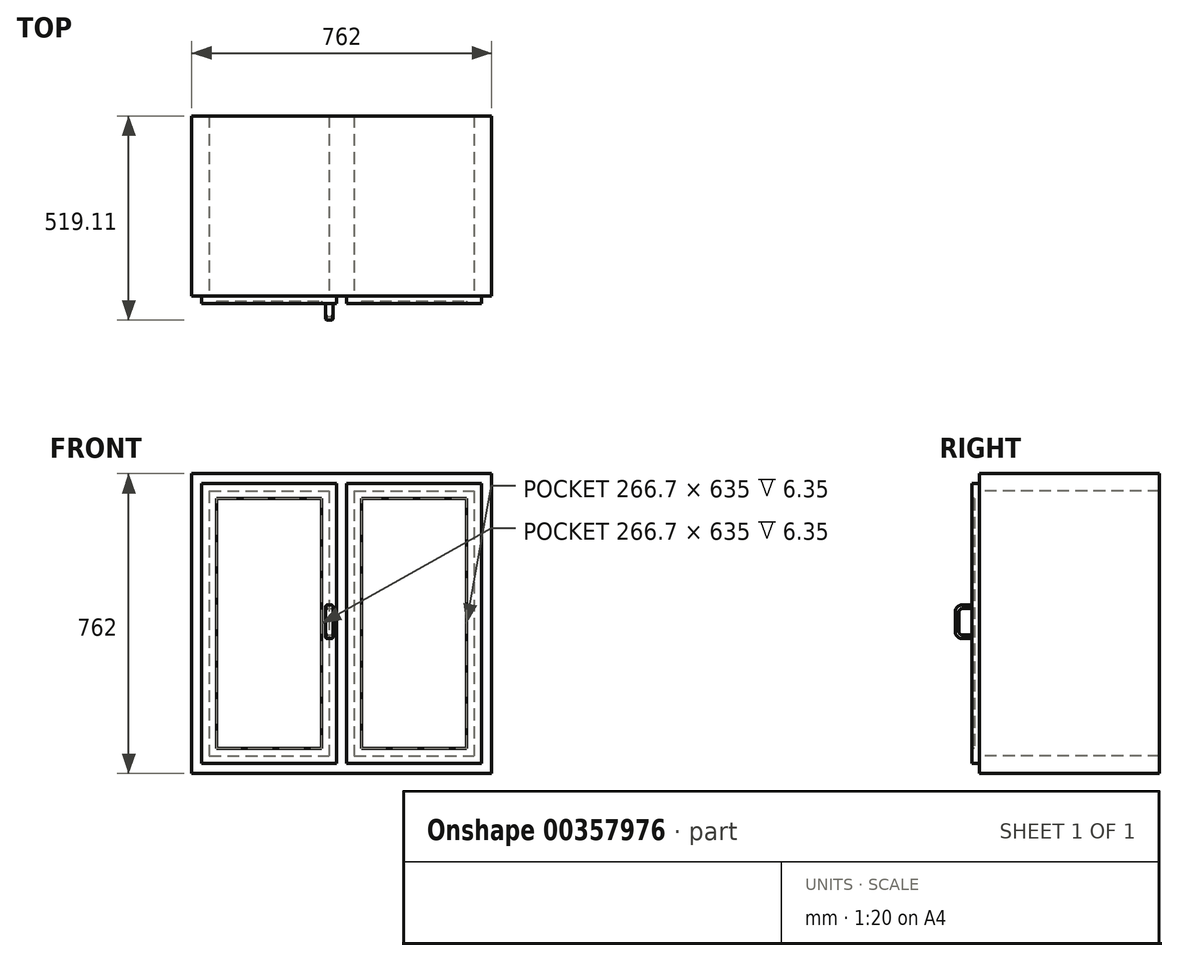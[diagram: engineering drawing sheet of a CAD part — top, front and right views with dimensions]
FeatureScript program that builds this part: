
annotation { "Feature Type Name" : "Feature", "Feature Type Description" : "" }
export const myFeature = defineFeature(function(context is Context, id is Id, definition is map)
    precondition{}
    {
        {
            var Q0;
            Q0=qCreatedBy(makeId("Top.planeOp"),FACE);
            var sketch = newSketch(context, id + "F0", { "sketchPlane" : qUnion([Q0])});
            skLineSegment(sketch, "E0.bottom", {"start": v(-381, 228.6) * mm, "end": v(381, 228.6) * mm});
            skLineSegment(sketch, "E0.top", {"start": v(-381, -228.6) * mm, "end": v(381, -228.6) * mm});
            skLineSegment(sketch, "E0.left", {"start": v(-381, 228.6) * mm, "end": v(-381, -228.6) * mm});
            skLineSegment(sketch, "E0.right", {"start": v(381, 228.6) * mm, "end": v(381, -228.6) * mm});
            skPoint(sketch, "E0.middle", {"position": v(0, 0) * mm});
            skSolve(sketch);
        }
        {
            var Q0;
            Q0 = qSketchRegion(id + "F0", true);
            extrude(context, id + "F1", {"entities" : qUnion([Q0]), "depth" : 381 * mm, "hasSecondDirection" : true, "secondDirectionOppositeDirection" : true, "secondDirectionDepth" : 381 * mm});
        }
        {
            var Q0;
            Q0=makeQuery(id+"F1.opExtrude","SWEPT_FACE",FACE,{"disambiguationData":[OSD([sQuery(id+"F0.wireOp",EDGE,"E0.top")])]});
            var sketch = newSketch(context, id + "F2", { "sketchPlane" : qUnion([Q0])});
            skLineSegment(sketch, "E1.bottom", {"start": v(-336.55, 336.55) * mm, "end": v(-31.75, 336.55) * mm});
            skLineSegment(sketch, "E1.top", {"start": v(-336.55, -336.55) * mm, "end": v(-31.75, -336.55) * mm});
            skLineSegment(sketch, "E1.left", {"start": v(-336.55, 336.55) * mm, "end": v(-336.55, -336.55) * mm});
            skLineSegment(sketch, "E1.right", {"start": v(-31.75, 336.55) * mm, "end": v(-31.75, -336.55) * mm});
            skPoint(sketch, "E1.middle", {"position": v(-184.15, 0) * mm});
            skLineSegment(sketch, "E2.bottom", {"start": v(31.75, 336.55) * mm, "end": v(336.55, 336.55) * mm});
            skLineSegment(sketch, "E2.top", {"start": v(31.75, -336.55) * mm, "end": v(336.55, -336.55) * mm});
            skLineSegment(sketch, "E2.left", {"start": v(31.75, 336.55) * mm, "end": v(31.75, -336.55) * mm});
            skLineSegment(sketch, "E2.right", {"start": v(336.55, 336.55) * mm, "end": v(336.55, -336.55) * mm});
            skPoint(sketch, "E2.middle", {"position": v(184.15, 0) * mm});
            skSolve(sketch);
        }
        {
            var Q0;
            Q0 = qSketchRegion(id + "F2", true);
            extrude(context, id + "F3", {"entities" : qUnion([Q0]), "operationType" : NewBodyOperationType.REMOVE, "endBound" : BoundingType.UP_TO_NEXT, "oppositeDirection" : true, "depth" : 25.4 * mm});
        }
        {
            var Q0;
            Q0=makeQuery(id+"F1.opExtrude","SWEPT_FACE",FACE,{"disambiguationData":[OSD([sQuery(id+"F0.wireOp",EDGE,"E0.top")])]});
            var sketch = newSketch(context, id + "F4", { "sketchPlane" : qUnion([Q0])});
            skLineSegment(sketch, "E3.bottom", {"start": v(-355.6, 355.6) * mm, "end": v(-12.7, 355.6) * mm});
            skLineSegment(sketch, "E3.top", {"start": v(-355.6, -355.6) * mm, "end": v(-12.7, -355.6) * mm});
            skLineSegment(sketch, "E3.left", {"start": v(-355.6, 355.6) * mm, "end": v(-355.6, -355.6) * mm});
            skLineSegment(sketch, "E3.right", {"start": v(-12.7, 355.6) * mm, "end": v(-12.7, -355.6) * mm});
            skPoint(sketch, "E3.middle", {"position": v(-184.15, 0) * mm});
            skLineSegment(sketch, "E4.bottom", {"start": v(12.7, 355.6) * mm, "end": v(355.6, 355.6) * mm});
            skLineSegment(sketch, "E4.top", {"start": v(12.7, -355.6) * mm, "end": v(355.6, -355.6) * mm});
            skLineSegment(sketch, "E4.left", {"start": v(12.7, 355.6) * mm, "end": v(12.7, -355.6) * mm});
            skLineSegment(sketch, "E4.right", {"start": v(355.6, 355.6) * mm, "end": v(355.6, -355.6) * mm});
            skPoint(sketch, "E4.middle", {"position": v(184.15, 0) * mm});
            skSolve(sketch);
        }
        {
            var Q0;
            Q0 = qSketchRegion(id + "F4", true);
            extrude(context, id + "F5", {"entities" : qUnion([Q0]), "operationType" : NewBodyOperationType.ADD, "depth" : 19.05 * mm});
        }
        {
            var Q0;
            Q0=makeQuery(id+"F5.opExtrude","CAP_FACE",FACE,{"disambiguationData":[OSD([sQuery(id+"F4.wireOp",EDGE,"E3.bottom"),sQuery(id+"F4.wireOp",EDGE,"E3.top"),sQuery(id+"F4.wireOp",EDGE,"E3.left"),sQuery(id+"F4.wireOp",EDGE,"E3.right")])],"isStart":false});
            var sketch = newSketch(context, id + "F6", { "sketchPlane" : qUnion([Q0])});
            skLineSegment(sketch, "E5.bottom", {"start": v(-317.5, 317.5) * mm, "end": v(-50.8, 317.5) * mm});
            skLineSegment(sketch, "E5.top", {"start": v(-317.5, -317.5) * mm, "end": v(-50.8, -317.5) * mm});
            skLineSegment(sketch, "E5.left", {"start": v(-317.5, 317.5) * mm, "end": v(-317.5, -317.5) * mm});
            skLineSegment(sketch, "E5.right", {"start": v(-50.8, 317.5) * mm, "end": v(-50.8, -317.5) * mm});
            skPoint(sketch, "E5.middle", {"position": v(-184.15, 0) * mm});
            skLineSegment(sketch, "E6.bottom", {"start": v(50.8, 317.5) * mm, "end": v(317.5, 317.5) * mm});
            skLineSegment(sketch, "E6.top", {"start": v(50.8, -317.5) * mm, "end": v(317.5, -317.5) * mm});
            skLineSegment(sketch, "E6.left", {"start": v(50.8, 317.5) * mm, "end": v(50.8, -317.5) * mm});
            skLineSegment(sketch, "E6.right", {"start": v(317.5, 317.5) * mm, "end": v(317.5, -317.5) * mm});
            skPoint(sketch, "E6.middle", {"position": v(184.15, 0) * mm});
            skSolve(sketch);
        }
        {
            var Q0;
            Q0 = qSketchRegion(id + "F6", true);
            extrude(context, id + "F7", {"entities" : qUnion([Q0]), "operationType" : NewBodyOperationType.REMOVE, "oppositeDirection" : true, "depth" : 6.35 * mm});
        }
        {
            var Q0;
            Q0=makeQuery(id+"F5.opExtrude","CAP_FACE",FACE,{"disambiguationData":[OSD([sQuery(id+"F4.wireOp",EDGE,"E3.bottom"),sQuery(id+"F4.wireOp",EDGE,"E3.top"),sQuery(id+"F4.wireOp",EDGE,"E3.left"),sQuery(id+"F4.wireOp",EDGE,"E3.right")])],"isStart":false});
            var sketch = newSketch(context, id + "F8", { "sketchPlane" : qUnion([Q0])});
            skArc(sketch, "E7", {"start": v(-36.51, 47.63) * mm, "mid": v(-41.28, 42.86) * mm, "end": v(-36.51, 38.1) * mm});
            skLineSegment(sketch, "E8", {"start": v(-36.51, 47.63) * mm, "end": v(-26.99, 47.63) * mm});
            skLineSegment(sketch, "E9", {"start": v(-36.51, 38.1) * mm, "end": v(-26.99, 38.1) * mm});
            skArc(sketch, "E10", {"start": v(-26.99, 38.1) * mm, "mid": v(-22.23, 42.86) * mm, "end": v(-26.99, 47.63) * mm});
            skLineSegment(sketch, "E11", {"start": v(-12.7, 0) * mm, "end": v(-50.8, 0) * mm, "construction": true});
            skLineSegment(sketch, "E12", {"start": v(-31.75, 0) * mm, "end": v(-31.75, 38.1) * mm, "construction": true});
            skLineSegment(sketch, "E13", {"start": v(-31.75, 38.1) * mm, "end": v(-31.75, 42.86) * mm, "construction": true});
            skLineSegment(sketch, "E14", {"start": v(-31.75, 42.86) * mm, "end": v(-31.75, 47.63) * mm, "construction": true});
            skSolve(sketch);
        }
        {
            var Q0;
            Q0=makeQuery(id+"F1.opExtrude","SWEPT_FACE",FACE,{"disambiguationData":[OSD([sQuery(id+"F0.wireOp",EDGE,"E0.left")])]});
            var Q1;
            Q1=sQuery(id+"F8.wireOp",VERTEX,"E12.end");
            cPlane(context, id + "F9", {"entities" : qUnion([Q0, Q1]), "cplaneType" : CPlaneType.PLANE_POINT, "offset" : 25.4 * mm, "width" : 152.4 * mm, "height" : 152.4 * mm});
        }
        {
            var Q0;
            Q0=qCreatedBy(id+"F9.planeOp",FACE);
            var sketch = newSketch(context, id + "F10", { "sketchPlane" : qUnion([Q0])});
            skLineSegment(sketch, "E15", {"start": v(247.65, 42.86) * mm, "end": v(273.05, 42.86) * mm});
            skLineSegment(sketch, "E16", {"start": v(285.75, 30.16) * mm, "end": v(285.75, -20.64) * mm});
            skLineSegment(sketch, "E17", {"start": v(273.05, -33.34) * mm, "end": v(247.65, -33.34) * mm});
            skPoint(sketch, "E18.visualSharp", {"position": v(285.75, 42.86) * mm});
            skArc(sketch, "E18.filletArc", {"start": v(285.75, 30.16) * mm, "mid": v(282.03, 39.14) * mm, "end": v(273.05, 42.86) * mm});
            skPoint(sketch, "E19.visualSharp", {"position": v(285.75, -33.34) * mm});
            skArc(sketch, "E19.filletArc", {"start": v(273.05, -33.34) * mm, "mid": v(282.03, -29.62) * mm, "end": v(285.75, -20.64) * mm});
            skSolve(sketch);
        }
        {
            var Q0;
            Q0=makeQuery(id+"F8.imprint","IMPRINT",FACE,{"disambiguationData":[TD([[makeQuery(id+"F8.imprint","IMPRINT",EDGE,{"derivedFrom":sQuery(id+"F8.wireOp",EDGE,"E7")}),1.0]])]});
            var Q1;
            Q1=sQuery(id+"F10.wireOp",EDGE,"E15");
            var Q2;
            Q2=sQuery(id+"F10.wireOp",EDGE,"E18.filletArc");
            var Q3;
            Q3=sQuery(id+"F10.wireOp",EDGE,"E16");
            var Q4;
            Q4=sQuery(id+"F10.wireOp",EDGE,"E19.filletArc");
            var Q5;
            Q5=sQuery(id+"F10.wireOp",EDGE,"E17");
            sweep(context, id + "F11", {"operationType" : NewBodyOperationType.ADD, "profiles" : qUnion([Q0]), "path" : qUnion([Q1, Q2, Q3, Q4, Q5])});
        }
    });
